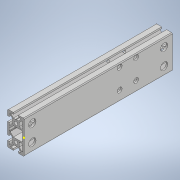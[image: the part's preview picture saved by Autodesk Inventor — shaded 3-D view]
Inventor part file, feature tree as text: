
AUTODESK INVENTOR PART (.ipt)
format: ipt  version: 2022 (Build 260153000, 153)  size: 443,392 bytes
history: native  units: mm
features: sketch x8, hole x7, other x7, extrude x1, pattern_linear x1
ambient origin geometry x8: Origin, YZ Plane, XZ Plane, XY Plane, X Axis, Y Axis, Z Axis, Center Point
bodies: Solid1 (feature_tree)
feature tree (24):
  extrude  "Extrusion1"  Depth=10.0mm TaperAngle=0.0deg
  hole  "Hole1"  [1 undecoded]
  pattern_linear  "Rectangular Pattern1"  Spacing1=101.0mm  [1 undecoded]
  hole  "Hole2"  [1 undecoded]
  hole  "Hole3"  [1 undecoded]
  hole  "Hole4"  [1 undecoded]
  hole  "Hole5"  [1 undecoded]
  other  "C1_XY"
  other  "C1_YZ"
  other  "C1_ZX"
  other  "C1_X"
  other  "C1_Y"
  other  "C1_Z"
  other  "C1_Center"
  hole  "穴8"  [1 undecoded]
  hole  "穴9"  [1 undecoded]
  sketch  "Sketch_63"  dims[d36=7.1mm d37=6.0mm d38=4.0mm d39=2.0mm d40=90.0deg d41=20.0mm d42=0.0mm d43=0.0mm d67=9.0mm d68=6.0mm d69=4.0mm d70=2.0mm d71=90.0deg d72=3.0mm d73=20.594885mm d74=101.0mm d75=101.0mm d76=6.0mm d77=6.0mm d78=8.0mm d79=4.0mm d80=90.0deg d81=8.0mm d82=20.594885mm]
  sketch  "Sketch2"  dims[d0=180.0mm d1=0.0mm]
  sketch  "Sketch3"  dims[d2=4.2mm d3=6.0mm d4=4.0mm d5=2.0mm d6=90.0deg d7=180.0mm d8=0.0mm d9=20.0mm d11=20.0mm d12=10.0mm d14=0.0mm]
  sketch  "Sketch4"  dims[d15=7.1mm d16=6.0mm d17=4.0mm d18=2.0mm d19=90.0deg d20=20.0mm d21=0.0mm]
  sketch  "Sketch5"  dims[d22=7.1mm d23=6.0mm d24=4.0mm d25=2.0mm d26=90.0deg d27=20.0mm d28=0.0mm]
  sketch  "Sketch6"  dims[d29=7.1mm d30=6.0mm d31=4.0mm d32=2.0mm d33=90.0deg d34=20.0mm d35=0.0mm]
  sketch  "スケッチ9"
  sketch  "スケッチ11"
note: 8 required parameter values undecoded (feature->parameter linkage not recoverable at this tier; creation-order binding heuristic only, values carry confidence <= 0.55)
